# Revit family: Water-Heater-Rinnai-TRW23-Wall-Mount-Rack-Unit
name_source: partatom
category: Mechanical Equipment
revit_build: Autodesk Revit MEP 2012 (Build: 20110309_2315(x64)
units: mm (PartAtom-declared; Revit-internal decimal feet)

## types (1)
- TRW23
    Applicable Altitude Range = 0-10,200ft (0-3,109m)
    Clearance for Back = 0"
    Clearance for Front = 0"
    Clearance for Ground or Bottom = 0"
    Clearance for Sides = 0"
    Clearance for Top = 0"
    Cold Water Connector = Cold Water Connection
    Cold Water Inlet Radius = 1"
    Cold Water Pipe = Metal - Rinnai - Bronze
    Combustibles = No
    Combustion Air = Indoor or outdoor
    Default Elevation = 0"
    Depth = 12 1/4"
    Description = Wall Hanging Tankless Water Heater
    Door = Metal - Rinnai - Aluminum - Polished Sliver
    Dry Weight = 3396.00 lb
    Electrical Consumption Range = Normal: 64 w, Standby: 2 w
    Exhaust Vent Length Note = 100 ft
    First Hour Rating = 0.00 GPM
    Flow Rate at 100 Deg F Rise = 7.60 GPM
    Flow Rate at 70 Deg F Rise = 10.80 GPM
    Frequency = 60 Hz
    Gas Connection = Gas Connection
    Gas Input Range = 15,200 - 398,000 BTU/h
    Gas Input Rate = 398000.0 Btu/h
    Gas Manifold Pressure High Fire = 0"
    Gas Manifold Pressure Low Fire = 0"
    Gas Pipe = Metal - Rinnai - Aluminum - Polished Sliver
    Gas Supply Pressure Max = 0"
    Gas Supply Pressure Min = 0"
    Gas Supply Radius = 5/8"
    Hardware = Metal - Rinnai - Aluminum Frame - Painted White
    Height = 57"
    Hot Water Connector = Hot Water Connection
    Hot Water Outlet Radius = 1"
    Hot Water Pipe = Metal - Rinnai - Bronze
    Installation Location = Indoor and outdoor
    Installation URL = https://www.rinnai.us
    Liquid Propane = No
    Manufacturer = Rinnai America Corporation
    Manufacturer Fax = 678-829-1666
    Max Amperage = 8 A
    Model = TRW23
    Natural Gas = No
    Panel = Metal - Rinnai - Aluminum Frame - Painted White
    Product Page URL = https://rinnai.us
    Recovery for 100 Deg Rise = 528-668 gal/h
    Spec Sheet URL = https://www.rinnai.us
    Storage Tank Volume = 100-300 gal
    Subcategory = Tankless Water Heaters
    Thermal Efficiency Rating = 0.96
    URL = https://rinnai.us
    Unit = Metal - Rinnai - Aluminum Frame - Painted White
    Vent Connector = Vent Connection
    Venting = Rinnai Common Vent System
    Voltage = 120 V
    Warranty = Commercial: 6-year on heat exchanger, 5-year on parts, up to 2 years labor
    Water Heater Model = RU98i (N or P)
    Water Supply Pressure Range = 0.00 psi
    Wattage = 64 W
    Weight Fully Assembled = 175.50 lb
    Width = 62"

## geometry (parser evidence)
native form markers: Blend x8, Sweep x17
no freeform markers — native parametric forms only
